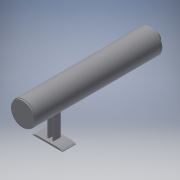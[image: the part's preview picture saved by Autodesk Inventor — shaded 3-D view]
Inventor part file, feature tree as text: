
AUTODESK INVENTOR PART (.ipt)
format: ipt  version: 2018.3 (Build 223284000, 284)  size: 215,040 bytes
history: native  units: mm
features: extrude x9, sketch x8, chamfer x5, fillet x2
ambient origin geometry x8: Origin, YZ Plane, XZ Plane, XY Plane, X Axis, Y Axis, Z Axis, Center Point
bodies: Solid1 (feature_tree)
feature tree (24):
  extrude  "Extrusion1"  Depth=12.5mm
  extrude  "Extrusion2"  Depth=5.5mm TaperAngle=0.0deg
  extrude  "Extrusion4"  Depth=3.0mm
  extrude  "Extrusion15"  Depth=1.25mm
  extrude  "Extrusion16"  Depth=1.5mm
  chamfer  "Chamfer4"  Distance=10.0mm
  extrude  "Extrusion17"  Depth=1.5mm
  chamfer  "Chamfer5"  Distance=40.0mm
  extrude  "Extrusion18"  Depth=1.5mm
  fillet  "Fillet4"  Radius=10.0mm
  fillet  "Fillet5"  Radius=1.0mm
  extrude  "Extrusion19"  Depth=4.9mm TaperAngle=45.0deg
  extrude  "Extrusion20"  Depth=1.5mm TaperAngle=0.0deg
  chamfer  "Chamfer6"  Distance=4.9mm Angle=45.0deg
  chamfer  "Chamfer7"  Distance=4.8mm
  chamfer  "Chamfer8"  Distance=3.0mm
  sketch  "Sketch2"  dims[d0=1.8mm d2=12.5mm]
  sketch  "Sketch4"  dims[d3=5.5mm d6=0.7mm d7=0.0mm]
  sketch  "Sketch15"  dims[d8=0.5mm d9=3.0mm]
  sketch  "Sketch16"  dims[d10=0.5mm d11=1.25mm]
  sketch  "Sketch17"  dims[d12=1.25mm d13=1.5mm]
  sketch  "Sketch18"  dims[d14=5.0mm]
  sketch  "Sketch19"  dims[d15=5.0mm d16=10.0mm d17=0.0mm]
  sketch  "Sketch20"  dims[d35=10.0mm d36=14.8mm d37=40.0mm d38=0.0mm d70=9.8mm d71=10.0mm d72=0.0mm d73=1.0mm d74=0.0mm d75=4.9mm d76=2.0mm d77=45.0deg d78=1.0mm d79=0.0mm d80=4.9mm d81=2.0mm d82=45.0deg d83=4.8mm d84=3.0mm d85=0.0mm d86=1.5mm d87=1.5mm d88=0.1mm d89=0.0mm d90=0.5mm d91=0.0mm d92=0.7mm d93=2.0mm d94=45.0deg d95=0.7mm d96=2.0mm d97=45.0deg d98=0.7mm d99=2.0mm d100=45.0deg]
